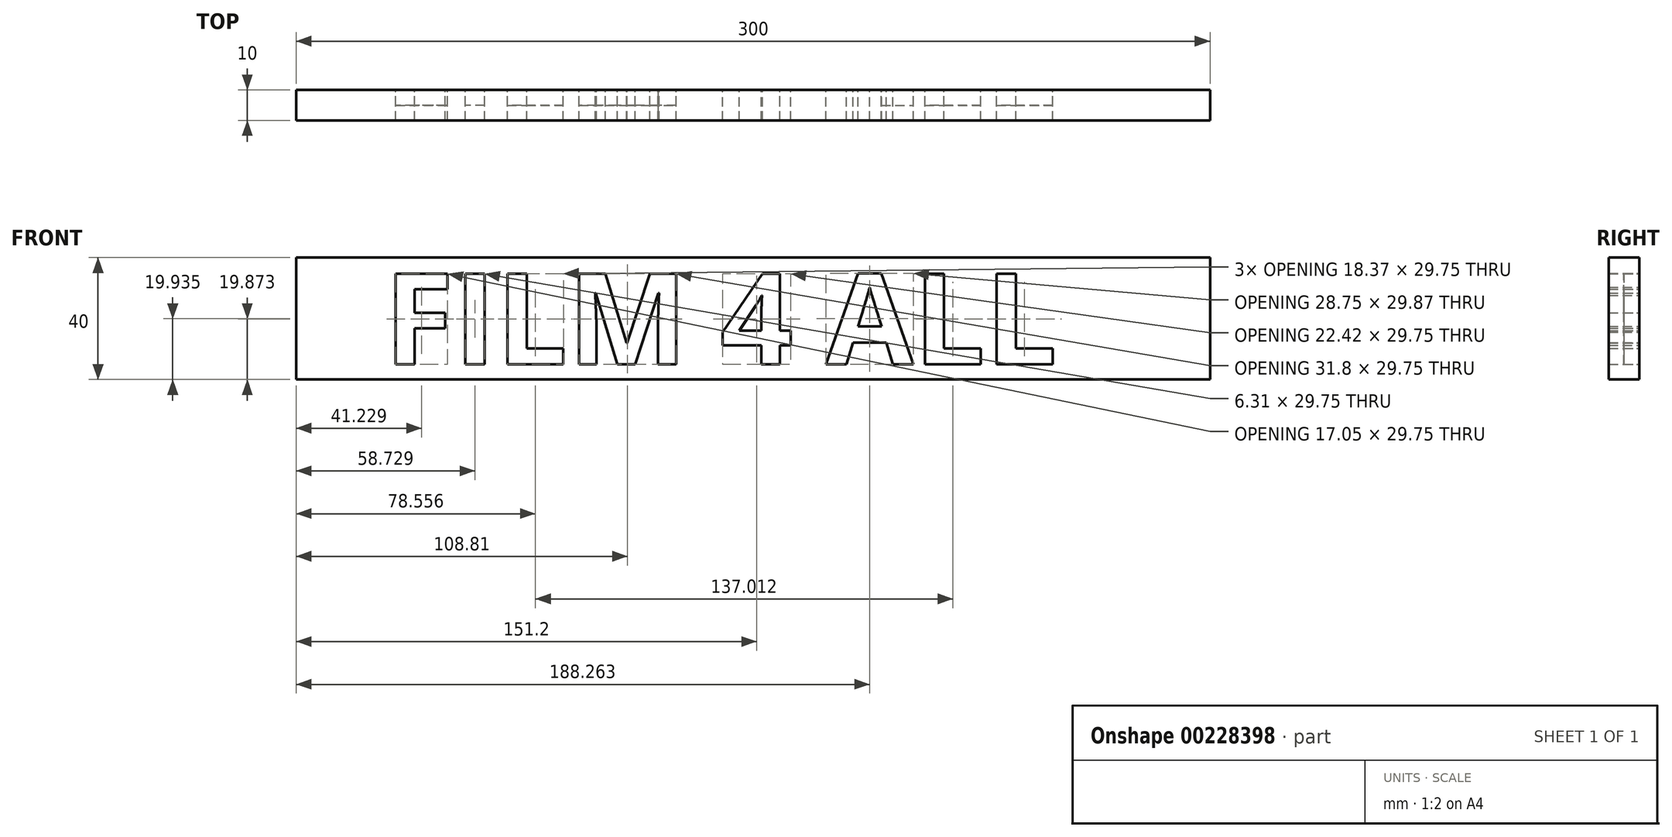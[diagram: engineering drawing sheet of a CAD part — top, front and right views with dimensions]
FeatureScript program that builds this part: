
annotation { "Feature Type Name" : "Feature", "Feature Type Description" : "" }
export const myFeature = defineFeature(function(context is Context, id is Id, definition is map)
    precondition{}
    {
        {
            var Q0;
            Q0=qCreatedBy(makeId("Front.planeOp"),FACE);
            var sketch = newSketch(context, id + "F0", { "sketchPlane" : qUnion([Q0])});
            skLineSegment(sketch, "E0.bottom", {"start": v(150, 20) * mm, "end": v(-150, 20) * mm});
            skLineSegment(sketch, "E0.top", {"start": v(150, -20) * mm, "end": v(-150, -20) * mm});
            skLineSegment(sketch, "E0.left", {"start": v(150, 20) * mm, "end": v(150, -20) * mm});
            skLineSegment(sketch, "E0.right", {"start": v(-150, 20) * mm, "end": v(-150, -20) * mm});
            skPoint(sketch, "E0.middle", {"position": v(0, 0) * mm});
            skText(sketch, "E1", { "text": "FILM 4 ALL", "fontName": "OpenSans-Bold.ttf"});
            skLineSegment(sketch, "E2", {"start": v(-121.04, 0) * mm, "end": v(101, 0) * mm, "construction": true});
            const initialGuessF0  = {"E1": [-0.12104, -0.015, 1, 0, 0.03]};
            skSetInitialGuess(sketch, initialGuessF0);
            skSolve(sketch);
        }
        {
            var Q0;
            Q0 = qSketchRegion(id + "F0", true);
            var Q1;
            Q1=makeQuery(id+"F0.imprint","IMPRINT",FACE,{"disambiguationData":[TD([[makeQuery(id+"F0.imprint","IMPRINT",EDGE,{"derivedFrom":sQuery(id+"F0.wireOp",EDGE,"E1.sketch_text.stroke-50")}),1.0]])]});
            var Q2;
            Q2=makeQuery(id+"F0.imprint","IMPRINT",FACE,{"disambiguationData":[TD([[makeQuery(id+"F0.imprint","IMPRINT",EDGE,{"derivedFrom":sQuery(id+"F0.wireOp",EDGE,"E1.sketch_text.stroke-65")}),1.0]])]});
            extrude(context, id + "F1", {"entities" : qUnion([Q0, Q1, Q2]), "depth" : 10 * mm});
        }
        {
            var Q0;
            Q0=makeQuery(id+"F1.opExtrude","CAP_FACE",FACE,{"disambiguationData":[OSD([sQuery(id+"F0.wireOp",EDGE,"E0.bottom"),sQuery(id+"F0.wireOp",EDGE,"E0.top"),sQuery(id+"F0.wireOp",EDGE,"E0.left"),sQuery(id+"F0.wireOp",EDGE,"E0.right"),sQuery(id+"F0.wireOp",EDGE,"E1.sketch_text.stroke-0"),sQuery(id+"F0.wireOp",EDGE,"E1.sketch_text.stroke-1"),sQuery(id+"F0.wireOp",EDGE,"E1.sketch_text.stroke-2"),sQuery(id+"F0.wireOp",EDGE,"E1.sketch_text.stroke-3"),sQuery(id+"F0.wireOp",EDGE,"E1.sketch_text.stroke-4"),sQuery(id+"F0.wireOp",EDGE,"E1.sketch_text.stroke-5"),sQuery(id+"F0.wireOp",EDGE,"E1.sketch_text.stroke-6"),sQuery(id+"F0.wireOp",EDGE,"E1.sketch_text.stroke-7"),sQuery(id+"F0.wireOp",EDGE,"E1.sketch_text.stroke-8"),sQuery(id+"F0.wireOp",EDGE,"E1.sketch_text.stroke-9"),sQuery(id+"F0.wireOp",EDGE,"E1.sketch_text.stroke-10"),sQuery(id+"F0.wireOp",EDGE,"E1.sketch_text.stroke-11"),sQuery(id+"F0.wireOp",EDGE,"E1.sketch_text.stroke-12"),sQuery(id+"F0.wireOp",EDGE,"E1.sketch_text.stroke-13"),sQuery(id+"F0.wireOp",EDGE,"E1.sketch_text.stroke-14"),sQuery(id+"F0.wireOp",EDGE,"E1.sketch_text.stroke-15"),sQuery(id+"F0.wireOp",EDGE,"E1.sketch_text.stroke-16"),sQuery(id+"F0.wireOp",EDGE,"E1.sketch_text.stroke-17"),sQuery(id+"F0.wireOp",EDGE,"E1.sketch_text.stroke-18"),sQuery(id+"F0.wireOp",EDGE,"E1.sketch_text.stroke-19"),sQuery(id+"F0.wireOp",EDGE,"E1.sketch_text.stroke-20"),sQuery(id+"F0.wireOp",EDGE,"E1.sketch_text.stroke-21"),sQuery(id+"F0.wireOp",EDGE,"E1.sketch_text.stroke-22"),sQuery(id+"F0.wireOp",EDGE,"E1.sketch_text.stroke-23"),sQuery(id+"F0.wireOp",EDGE,"E1.sketch_text.stroke-24"),sQuery(id+"F0.wireOp",EDGE,"E1.sketch_text.stroke-25"),sQuery(id+"F0.wireOp",EDGE,"E1.sketch_text.stroke-26"),sQuery(id+"F0.wireOp",EDGE,"E1.sketch_text.stroke-27"),sQuery(id+"F0.wireOp",EDGE,"E1.sketch_text.stroke-28"),sQuery(id+"F0.wireOp",EDGE,"E1.sketch_text.stroke-29"),sQuery(id+"F0.wireOp",EDGE,"E1.sketch_text.stroke-30"),sQuery(id+"F0.wireOp",EDGE,"E1.sketch_text.stroke-31"),sQuery(id+"F0.wireOp",EDGE,"E1.sketch_text.stroke-32"),sQuery(id+"F0.wireOp",EDGE,"E1.sketch_text.stroke-33"),sQuery(id+"F0.wireOp",EDGE,"E1.sketch_text.stroke-34"),sQuery(id+"F0.wireOp",EDGE,"E1.sketch_text.stroke-35"),sQuery(id+"F0.wireOp",EDGE,"E1.sketch_text.stroke-36"),sQuery(id+"F0.wireOp",EDGE,"E1.sketch_text.stroke-37"),sQuery(id+"F0.wireOp",EDGE,"E1.sketch_text.stroke-38"),sQuery(id+"F0.wireOp",EDGE,"E1.sketch_text.stroke-39"),sQuery(id+"F0.wireOp",EDGE,"E1.sketch_text.stroke-40"),sQuery(id+"F0.wireOp",EDGE,"E1.sketch_text.stroke-41"),sQuery(id+"F0.wireOp",EDGE,"E1.sketch_text.stroke-42"),sQuery(id+"F0.wireOp",EDGE,"E1.sketch_text.stroke-43"),sQuery(id+"F0.wireOp",EDGE,"E1.sketch_text.stroke-44"),sQuery(id+"F0.wireOp",EDGE,"E1.sketch_text.stroke-45"),sQuery(id+"F0.wireOp",EDGE,"E1.sketch_text.stroke-46"),sQuery(id+"F0.wireOp",EDGE,"E1.sketch_text.stroke-47"),sQuery(id+"F0.wireOp",EDGE,"E1.sketch_text.stroke-48"),sQuery(id+"F0.wireOp",EDGE,"E1.sketch_text.stroke-49"),sQuery(id+"F0.wireOp",EDGE,"E1.sketch_text.stroke-57"),sQuery(id+"F0.wireOp",EDGE,"E1.sketch_text.stroke-58"),sQuery(id+"F0.wireOp",EDGE,"E1.sketch_text.stroke-59"),sQuery(id+"F0.wireOp",EDGE,"E1.sketch_text.stroke-60"),sQuery(id+"F0.wireOp",EDGE,"E1.sketch_text.stroke-61"),sQuery(id+"F0.wireOp",EDGE,"E1.sketch_text.stroke-62"),sQuery(id+"F0.wireOp",EDGE,"E1.sketch_text.stroke-63"),sQuery(id+"F0.wireOp",EDGE,"E1.sketch_text.stroke-64"),sQuery(id+"F0.wireOp",EDGE,"E1.sketch_text.stroke-69"),sQuery(id+"F0.wireOp",EDGE,"E1.sketch_text.stroke-70"),sQuery(id+"F0.wireOp",EDGE,"E1.sketch_text.stroke-71"),sQuery(id+"F0.wireOp",EDGE,"E1.sketch_text.stroke-72"),sQuery(id+"F0.wireOp",EDGE,"E1.sketch_text.stroke-73"),sQuery(id+"F0.wireOp",EDGE,"E1.sketch_text.stroke-74"),sQuery(id+"F0.wireOp",EDGE,"E1.sketch_text.stroke-75"),sQuery(id+"F0.wireOp",EDGE,"E1.sketch_text.stroke-76"),sQuery(id+"F0.wireOp",EDGE,"E1.sketch_text.stroke-77"),sQuery(id+"F0.wireOp",EDGE,"E1.sketch_text.stroke-78"),sQuery(id+"F0.wireOp",EDGE,"E1.sketch_text.stroke-79"),sQuery(id+"F0.wireOp",EDGE,"E1.sketch_text.stroke-80")])],"isStart":true});
            var sketch = newSketch(context, id + "F2", { "sketchPlane" : qUnion([Q0])});
            skLineSegment(sketch, "E3.bottom", {"start": v(-150, 20) * mm, "end": v(150, 20) * mm});
            skLineSegment(sketch, "E3.top", {"start": v(-150, -20) * mm, "end": v(150, -20) * mm});
            skLineSegment(sketch, "E3.left", {"start": v(-150, 20) * mm, "end": v(-150, -20) * mm});
            skLineSegment(sketch, "E3.right", {"start": v(150, 20) * mm, "end": v(150, -20) * mm});
            skSolve(sketch);
        }
        {
            var Q0;
            Q0=makeQuery(id+"F2.imprint","IMPRINT",FACE,{"disambiguationData":[TD([[makeQuery(id+"F2.imprint","IMPRINT",EDGE,{"derivedFrom":sQuery(id+"F2.wireOp",EDGE,"E3.bottom")}),-1.0]])]});
            var sketch = newSketch(context, id + "F3", { "sketchPlane" : qUnion([Q0])});
            skLineSegment(sketch, "E4.0.0", {"start": v(-150, 20) * mm, "end": v(-150, -20) * mm});
            skLineSegment(sketch, "E4.0.1", {"start": v(-150, -20) * mm, "end": v(150, -20) * mm});
            skLineSegment(sketch, "E4.0.2", {"start": v(150, -20) * mm, "end": v(150, 20) * mm});
            skLineSegment(sketch, "E4.0.3", {"start": v(150, 20) * mm, "end": v(-150, 20) * mm});
            skLineSegment(sketch, "E5.0", {"start": v(117.3, -15) * mm, "end": v(117.3, 14.75) * mm});
            skLineSegment(sketch, "E5.1.0", {"start": v(101, 1.9) * mm, "end": v(101, -3.24) * mm});
            skLineSegment(sketch, "E5.1.1", {"start": v(101, -3.24) * mm, "end": v(111.09, -3.24) * mm});
            skLineSegment(sketch, "E5.1.2", {"start": v(111.09, -3.24) * mm, "end": v(111.09, -15) * mm});
            skLineSegment(sketch, "E5.1.3", {"start": v(111.09, -15) * mm, "end": v(117.3, -15) * mm});
            skLineSegment(sketch, "E5.1.4", {"start": v(117.3, -15) * mm, "end": v(117.3, 14.75) * mm});
            skLineSegment(sketch, "E5.1.5", {"start": v(117.3, 14.75) * mm, "end": v(100.24, 14.75) * mm});
            skLineSegment(sketch, "E5.1.6", {"start": v(100.24, 14.75) * mm, "end": v(100.24, 9.58) * mm});
            skLineSegment(sketch, "E5.1.7", {"start": v(100.24, 9.58) * mm, "end": v(111.09, 9.58) * mm});
            skLineSegment(sketch, "E5.1.8", {"start": v(111.09, 9.58) * mm, "end": v(111.09, 1.9) * mm});
            skLineSegment(sketch, "E5.1.9", {"start": v(111.09, 1.9) * mm, "end": v(101, 1.9) * mm});
            skLineSegment(sketch, "E6.0.0", {"start": v(94.42, 14.75) * mm, "end": v(88.11, 14.75) * mm});
            skLineSegment(sketch, "E6.0.1", {"start": v(88.11, 14.75) * mm, "end": v(88.11, -15) * mm});
            skLineSegment(sketch, "E6.0.2", {"start": v(88.11, -15) * mm, "end": v(94.42, -15) * mm});
            skLineSegment(sketch, "E6.0.3", {"start": v(94.42, -15) * mm, "end": v(94.42, 14.75) * mm});
            skLineSegment(sketch, "E6.1.0", {"start": v(74.32, -9.8) * mm, "end": v(62.26, -9.8) * mm});
            skLineSegment(sketch, "E6.1.1", {"start": v(62.26, -9.8) * mm, "end": v(62.26, -15) * mm});
            skLineSegment(sketch, "E6.1.2", {"start": v(62.26, -15) * mm, "end": v(80.63, -15) * mm});
            skLineSegment(sketch, "E6.1.3", {"start": v(80.63, -15) * mm, "end": v(80.63, 14.75) * mm});
            skLineSegment(sketch, "E6.1.4", {"start": v(80.63, 14.75) * mm, "end": v(74.32, 14.75) * mm});
            skLineSegment(sketch, "E6.1.5", {"start": v(74.32, 14.75) * mm, "end": v(74.32, -9.8) * mm});
            skLineSegment(sketch, "E6.2.0", {"start": v(30.86, 8.3) * mm, "end": v(31.04, 8.3) * mm});
            skLineSegment(sketch, "E6.2.1", {"start": v(31.04, 8.3) * mm, "end": v(38.71, -15) * mm});
            skLineSegment(sketch, "E6.2.2", {"start": v(38.71, -15) * mm, "end": v(44.5, -15) * mm});
            skLineSegment(sketch, "E6.2.3", {"start": v(44.5, -15) * mm, "end": v(51.66, 8.33) * mm});
            skLineSegment(sketch, "E6.2.4", {"start": v(51.66, 8.33) * mm, "end": v(51.84, 8.33) * mm});
            skFitSpline(sketch, "E6.2.5", {"points": [v(51.84, 8.33) * mm, v(51.45, 1.22) * mm, v(51.45, -1.17) * mm]});
            skLineSegment(sketch, "E6.2.6", {"start": v(51.45, -1.17) * mm, "end": v(51.45, -15) * mm});
            skLineSegment(sketch, "E6.2.7", {"start": v(51.45, -15) * mm, "end": v(57.09, -15) * mm});
            skLineSegment(sketch, "E6.2.8", {"start": v(57.09, -15) * mm, "end": v(57.09, 14.75) * mm});
            skLineSegment(sketch, "E6.2.9", {"start": v(57.09, 14.75) * mm, "end": v(48.5, 14.75) * mm});
            skLineSegment(sketch, "E6.2.10", {"start": v(48.5, 14.75) * mm, "end": v(41.46, -8) * mm});
            skLineSegment(sketch, "E6.2.11", {"start": v(41.46, -8) * mm, "end": v(41.34, -8) * mm});
            skLineSegment(sketch, "E6.2.12", {"start": v(41.34, -8) * mm, "end": v(33.87, 14.75) * mm});
            skLineSegment(sketch, "E6.2.13", {"start": v(33.87, 14.75) * mm, "end": v(25.29, 14.75) * mm});
            skLineSegment(sketch, "E6.2.14", {"start": v(25.29, 14.75) * mm, "end": v(25.29, -15) * mm});
            skLineSegment(sketch, "E6.2.15", {"start": v(25.29, -15) * mm, "end": v(31.17, -15) * mm});
            skLineSegment(sketch, "E6.2.16", {"start": v(31.17, -15) * mm, "end": v(31.17, -0.92) * mm});
            skFitSpline(sketch, "E6.2.17", {"points": [v(31.17, -0.92) * mm, v(31.17, 0.08) * mm, v(31.14, 1.38) * mm]});
            skFitSpline(sketch, "E6.2.18", {"points": [v(31.14, 1.38) * mm, v(31.1, 2.68) * mm, v(30.86, 8.3) * mm]});
            skLineSegment(sketch, "E6.3.0", {"start": v(-34.4, 14.87) * mm, "end": v(-42.1, 14.87) * mm});
            skLineSegment(sketch, "E6.3.1", {"start": v(-42.1, 14.87) * mm, "end": v(-52.64, -15) * mm});
            skLineSegment(sketch, "E6.3.2", {"start": v(-52.64, -15) * mm, "end": v(-45.84, -15) * mm});
            skLineSegment(sketch, "E6.3.3", {"start": v(-45.84, -15) * mm, "end": v(-43.69, -7.92) * mm});
            skLineSegment(sketch, "E6.3.4", {"start": v(-43.69, -7.92) * mm, "end": v(-32.84, -7.92) * mm});
            skLineSegment(sketch, "E6.3.5", {"start": v(-32.84, -7.92) * mm, "end": v(-30.69, -15) * mm});
            skLineSegment(sketch, "E6.3.6", {"start": v(-30.69, -15) * mm, "end": v(-23.9, -15) * mm});
            skLineSegment(sketch, "E6.3.7", {"start": v(-23.9, -15) * mm, "end": v(-34.4, 14.87) * mm});
            skLineSegment(sketch, "E7.0.0", {"start": v(-8.83, 14.75) * mm, "end": v(-8.83, -3.95) * mm});
            skLineSegment(sketch, "E7.0.1", {"start": v(-8.83, -3.95) * mm, "end": v(-12.41, -3.95) * mm});
            skLineSegment(sketch, "E7.0.2", {"start": v(-12.41, -3.95) * mm, "end": v(-12.41, -8.83) * mm});
            skLineSegment(sketch, "E7.0.3", {"start": v(-12.41, -8.83) * mm, "end": v(-8.83, -8.83) * mm});
            skLineSegment(sketch, "E7.0.4", {"start": v(-8.83, -8.83) * mm, "end": v(-8.83, -15) * mm});
            skLineSegment(sketch, "E7.0.5", {"start": v(-8.83, -15) * mm, "end": v(-2.69, -15) * mm});
            skLineSegment(sketch, "E7.0.6", {"start": v(-2.69, -15) * mm, "end": v(-2.69, -8.83) * mm});
            skLineSegment(sketch, "E7.0.7", {"start": v(-2.69, -8.83) * mm, "end": v(10, -8.83) * mm});
            skLineSegment(sketch, "E7.0.8", {"start": v(10, -8.83) * mm, "end": v(10, -4.46) * mm});
            skLineSegment(sketch, "E7.0.9", {"start": v(10, -4.46) * mm, "end": v(-3.04, 14.75) * mm});
            skLineSegment(sketch, "E7.0.10", {"start": v(-3.04, 14.75) * mm, "end": v(-8.83, 14.75) * mm});
            skLineSegment(sketch, "E8.0", {"start": v(-2.69, -3.95) * mm, "end": v(-2.69, 1.1) * mm});
            skPoint(sketch, "E8.1", {"position": v(0.9, -3.95) * mm});
            skFitSpline(sketch, "E9.0", {"points": [v(-2.69, 1.1) * mm, v(-2.69, 2.36) * mm, v(-2.8, 4.76) * mm]});
            skFitSpline(sketch, "E9.1", {"points": [v(-2.8, 4.76) * mm, v(-2.9, 7.15) * mm, v(-2.95, 7.55) * mm]});
            skLineSegment(sketch, "E9.2", {"start": v(-2.95, 7.55) * mm, "end": v(-2.8, 7.55) * mm});
            skFitSpline(sketch, "E9.3", {"points": [v(-2.8, 7.55) * mm, v(-2.04, 5.87) * mm, v(-0.98, 4.3) * mm]});
            skLineSegment(sketch, "E9.4", {"start": v(-0.98, 4.3) * mm, "end": v(4.48, -3.95) * mm});
            skLineSegment(sketch, "E9.5", {"start": v(4.48, -3.95) * mm, "end": v(-2.69, -3.95) * mm});
            skPoint(sketch, "E9.6", {"position": v(-2.86, 6.15) * mm});
            skFitSpline(sketch, "E10.1", {"points": [v(-38.27, 10.25) * mm, v(-37.6, 7.64) * mm, v(-34.43, -2.63) * mm]});
            skLineSegment(sketch, "E10.2", {"start": v(-34.43, -2.63) * mm, "end": v(-42.18, -2.63) * mm});
            skFitSpline(sketch, "E10.3", {"points": [v(-42.18, -2.63) * mm, v(-39.2, 7) * mm, v(-38.81, 8.26) * mm]});
            skFitSpline(sketch, "E10.4", {"points": [v(-38.81, 8.26) * mm, v(-38.43, 9.52) * mm, v(-38.27, 10.25) * mm]});
            skLineSegment(sketch, "E11.0.0", {"start": v(-62.7, -9.8) * mm, "end": v(-74.76, -9.8) * mm});
            skLineSegment(sketch, "E11.0.1", {"start": v(-74.76, -9.8) * mm, "end": v(-74.76, -15) * mm});
            skLineSegment(sketch, "E11.0.2", {"start": v(-74.76, -15) * mm, "end": v(-56.38, -15) * mm});
            skLineSegment(sketch, "E11.0.3", {"start": v(-56.38, -15) * mm, "end": v(-56.38, 14.75) * mm});
            skLineSegment(sketch, "E11.0.4", {"start": v(-56.38, 14.75) * mm, "end": v(-62.7, 14.75) * mm});
            skLineSegment(sketch, "E11.0.5", {"start": v(-62.7, 14.75) * mm, "end": v(-62.7, -9.8) * mm});
            skLineSegment(sketch, "E12.0.0", {"start": v(-86.23, -9.8) * mm, "end": v(-98.3, -9.8) * mm});
            skLineSegment(sketch, "E12.0.1", {"start": v(-98.3, -9.8) * mm, "end": v(-98.3, -15) * mm});
            skLineSegment(sketch, "E12.0.2", {"start": v(-98.3, -15) * mm, "end": v(-79.93, -15) * mm});
            skLineSegment(sketch, "E12.0.3", {"start": v(-79.93, -15) * mm, "end": v(-79.93, 14.75) * mm});
            skLineSegment(sketch, "E12.0.4", {"start": v(-79.93, 14.75) * mm, "end": v(-86.23, 14.75) * mm});
            skLineSegment(sketch, "E12.0.5", {"start": v(-86.23, 14.75) * mm, "end": v(-86.23, -9.8) * mm});
            skSolve(sketch);
        }
        {
            var Q0;
            Q0 = qSketchRegion(id + "FY5jhTokOIBYWNL_3", true);
            var Q1;
            Q1=makeQuery(id+"F2.imprint","IMPRINT",FACE,{"disambiguationData":[TD([[makeQuery(id+"F2.imprint","IMPRINT",EDGE,{"derivedFrom":makeQuery(id+"F1.opExtrude","CAP_EDGE",EDGE,{"disambiguationData":[OSD([sQuery(id+"F0.wireOp",EDGE,"E1.sketch_text.stroke-75")])],"isStart":true})}),1.0]])]});
            var Q2;
            Q2=makeQuery(id+"F2.imprint","IMPRINT",FACE,{"disambiguationData":[TD([[makeQuery(id+"F2.imprint","IMPRINT",EDGE,{"derivedFrom":makeQuery(id+"F1.opExtrude","CAP_EDGE",EDGE,{"disambiguationData":[OSD([sQuery(id+"F0.wireOp",EDGE,"E1.sketch_text.stroke-69")])],"isStart":true})}),1.0]])]});
            var Q3;
            Q3=makeQuery(id+"F3.imprint","IMPRINT",FACE,{"disambiguationData":[TD([[makeQuery(id+"F3.imprint","IMPRINT",EDGE,{"derivedFrom":sQuery(id+"F3.wireOp",EDGE,"E6.3.0")}),1.0]])]});
            var Q4;
            Q4=makeQuery(id+"F3.imprint","IMPRINT",FACE,{"disambiguationData":[TD([[makeQuery(id+"F3.imprint","IMPRINT",EDGE,{"derivedFrom":sQuery(id+"F3.wireOp",EDGE,"E7.0.0")}),1.0]])]});
            var Q5;
            Q5=makeQuery(id+"F2.imprint","IMPRINT",FACE,{"disambiguationData":[TD([[makeQuery(id+"F2.imprint","IMPRINT",EDGE,{"derivedFrom":makeQuery(id+"F1.opExtrude","CAP_EDGE",EDGE,{"disambiguationData":[OSD([sQuery(id+"F0.wireOp",EDGE,"E1.sketch_text.stroke-20")])],"isStart":true})}),1.0]])]});
            var Q6;
            Q6=makeQuery(id+"F2.imprint","IMPRINT",FACE,{"disambiguationData":[TD([[makeQuery(id+"F2.imprint","IMPRINT",EDGE,{"derivedFrom":makeQuery(id+"F1.opExtrude","CAP_EDGE",EDGE,{"disambiguationData":[OSD([sQuery(id+"F0.wireOp",EDGE,"E1.sketch_text.stroke-14")])],"isStart":true})}),1.0]])]});
            var Q7;
            Q7=makeQuery(id+"F2.imprint","IMPRINT",FACE,{"disambiguationData":[TD([[makeQuery(id+"F2.imprint","IMPRINT",EDGE,{"derivedFrom":makeQuery(id+"F1.opExtrude","CAP_EDGE",EDGE,{"disambiguationData":[OSD([sQuery(id+"F0.wireOp",EDGE,"E1.sketch_text.stroke-10")])],"isStart":true})}),1.0]])]});
            var Q8;
            Q8=makeQuery(id+"F2.imprint","IMPRINT",FACE,{"disambiguationData":[TD([[makeQuery(id+"F2.imprint","IMPRINT",EDGE,{"derivedFrom":makeQuery(id+"F1.opExtrude","CAP_EDGE",EDGE,{"disambiguationData":[OSD([sQuery(id+"F0.wireOp",EDGE,"E1.sketch_text.stroke-0")])],"isStart":true})}),1.0]])]});
            extrude(context, id + "F4", {"entities" : qUnion([Q0, Q1, Q2, Q3, Q4, Q5, Q6, Q7, Q8]), "oppositeDirection" : true, "depth" : 5 * mm});
        }
    });
